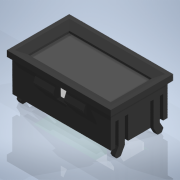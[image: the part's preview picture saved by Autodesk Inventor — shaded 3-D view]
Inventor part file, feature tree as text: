
AUTODESK INVENTOR PART (.ipt)
format: ipt  version: 2022 (Build 260153000, 153)  size: 489,984 bytes
history: native  units: in
note: dims shown in document units (in); Inventor stores cm internally (conversion verified against a paired STEP export)
features: sketch x14, extrude x13, plane x5, loft x4, mirror x4, other x4, projected_geometry x3, chamfer x2
ambient origin geometry x8: Origin, YZ Plane, XZ Plane, XY Plane, X Axis, Y Axis, Z Axis, Center Point
bodies: Solid1 (feature_tree)
feature tree (49):
  extrude  "Extrusion1"  Depth=1.131in
  chamfer  "Chamfer1"  Distance=0.105in
  extrude  "Extrusion2"  Depth=1.783in
  extrude  "Extrusion3"  Depth=0.082in
  extrude  "Extrusion4"  Depth=0.082in
  sketch  "Sketch5"  dims[d12=0.082in d13=0.167in d14=0.0in]
  loft  "Loft1"
  loft  "Loft2"
  extrude  "Extrusion5"  Depth=0.91in
  plane  "Work Plane1"
  mirror  "Mirror1"
  extrude  "Extrusion6"  Depth=0.36in
  extrude  "Extrusion7"  Depth=0.055in TaperAngle=0.0deg
  sketch  "Sketch10"  dims[d23=0.36in d24=0.055in d25=0.0in]
  loft  "Loft3"
  loft  "Loft4"
  mirror  "Mirror2"
  extrude  "Extrusion8"  TaperAngle=0.0deg  [1 undecoded]
  extrude  "Extrusion9"  Depth=0.433in
  plane  "Work Plane2"
  mirror  "Mirror3"
  mirror  "Mirror4"
  extrude  "Extrusion10"  Depth=0.201in
  sketch  "Sketch16"  dims[d36=0.055in d37=0.0in d38=0.433in]
  extrude  "Extrusion11"  Depth=0.201in
  extrude  "Extrusion12"  Depth=0.201in
  extrude  "Extrusion13"  Depth=0.201in
  chamfer  "Chamfer2"  Distance=0.417in
  sketch  "Sketch1"  dims[d0=1.881in d1=1.131in d2=0.105in d3=0.0in]
  sketch  "Sketch2"  dims[d4=0.12in d5=0.125in d6=30.0deg d7=1.783in]
  sketch  "Sketch3"  dims[d8=1.03in d9=0.082in]
  sketch  "Sketch4"  dims[d10=0.082in d11=0.082in]
  other  "Edges1"
  other  "Edges2"
  sketch  "Sketch6"  dims[d15=0.179in d16=0.455in]
  sketch  "Sketch7"  dims[d17=0.91in d19=0.025in]
  sketch  "Sketch9"  dims[d20=0.055in d21=0.0in d22=0.36in]
  projected_geometry  "Projected Loop1"
  projected_geometry  "Projected Loop2"
  other  "Edges3"
  other  "Edges4"
  sketch  "Sketch12"  dims[d26=0.13in d27=0.13in]
  sketch  "Sketch13"  dims[d28=0.0in d29=90.0deg d30=0.0in d31=90.0deg]
  plane  "Work Plane3"
  plane  "Work Plane4"
  plane  "Work Plane5"
  sketch  "Sketch15"  dims[d32=0.0in d33=90.0deg d34=0.0in d35=90.0deg]
  projected_geometry  "Projected Loop3"
  sketch  "Sketch17"  dims[d39=1.0in d40=0.0in d41=0.201in d42=0.201in d43=0.201in d44=0.201in d45=0.417in d46=0.0in d47=0.077in d48=0.077in d49=0.0in d50=90.0deg d51=0.0in d52=90.0deg d53=0.0in d54=90.0deg d55=0.0in d56=90.0deg d57=0.0in d58=0.0in d59=0.59in d60=0.058in d61=0.058in d63=0.058in d64=0.065in d65=0.114in d66=1.0in d67=0.0in d68=-0.8915in d69=0.365in d70=0.0in d71=0.32in d72=0.32in d73=0.23in d74=0.4in d75=0.275in d76=0.0in d77=0.11in d78=0.0in d79=0.0591in d80=0.0591in d81=0.075in d82=0.075in d83=0.0591in d84=0.0591in d85=0.295in d86=0.0in d87=0.012in d88=0.125in d89=30.0deg]
note: 1 required parameter value undecoded (feature->parameter linkage not recoverable at this tier; creation-order binding heuristic only, values carry confidence <= 0.55)
